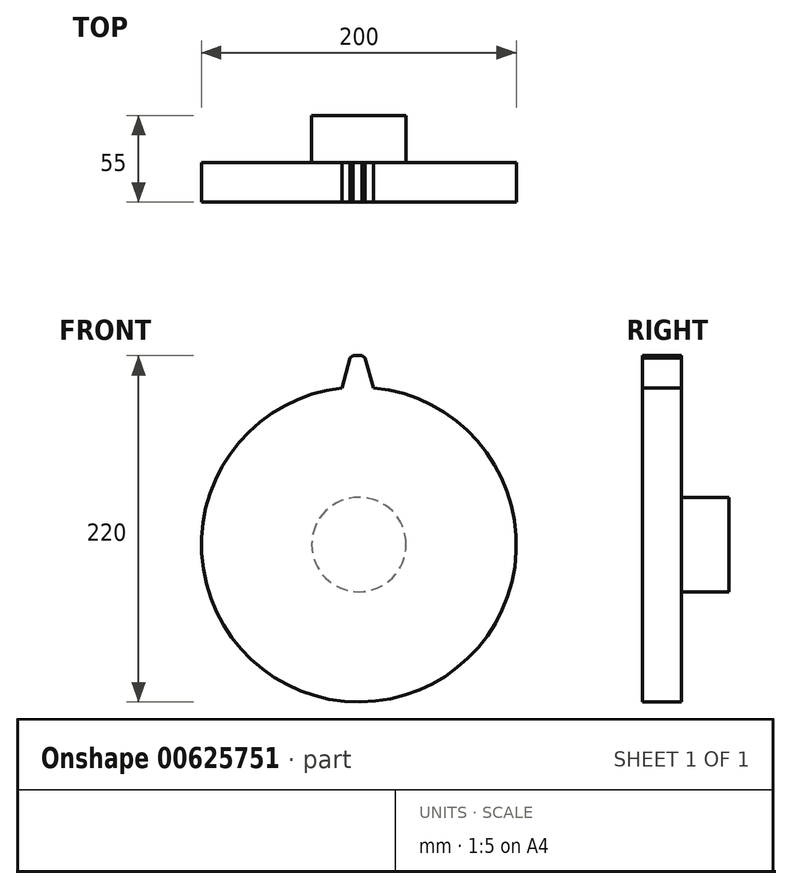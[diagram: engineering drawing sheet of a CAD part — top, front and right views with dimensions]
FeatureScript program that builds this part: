
annotation { "Feature Type Name" : "Feature", "Feature Type Description" : "" }
export const myFeature = defineFeature(function(context is Context, id is Id, definition is map)
    precondition{}
    {
        {
            var Q0;
            Q0=qCreatedBy(makeId("Front.planeOp"),FACE);
            var sketch = newSketch(context, id + "F0", { "sketchPlane" : qUnion([Q0])});
            skCircle(sketch, "E0", {"center": v(0, 0) * mm, "radius": 100 * mm});
            skSolve(sketch);
        }
        {
            var Q0;
            Q0 = qSketchRegion(id + "F0", true);
            extrude(context, id + "F1", {"entities" : qUnion([Q0]), "depth" : 25 * mm, "offsetDistance" : 25 * mm});
        }
        {
            var Q0;
            Q0=makeQuery(id+"F1.opExtrude","CAP_FACE",FACE,{"disambiguationData":[OSD([sQuery(id+"F0.wireOp",EDGE,"E0")])],"isStart":true});
            var sketch = newSketch(context, id + "F2", { "sketchPlane" : qUnion([Q0])});
            skCircle(sketch, "E1", {"center": v(0, 0) * mm, "radius": 30 * mm});
            skSolve(sketch);
        }
        {
            var Q0;
            Q0 = qSketchRegion(id + "F2", true);
            extrude(context, id + "F3", {"entities" : qUnion([Q0]), "operationType" : NewBodyOperationType.ADD, "depth" : 30 * mm, "offsetDistance" : 25 * mm});
        }
        {
            var Q0;
            Q0=makeQuery(id+"F1.opExtrude","CAP_FACE",FACE,{"disambiguationData":[OSD([sQuery(id+"F0.wireOp",EDGE,"E0")])],"isStart":true});
            var sketch = newSketch(context, id + "F4", { "sketchPlane" : qUnion([Q0])});
            skLineSegment(sketch, "E2", {"start": v(-9.33, 99.56) * mm, "end": v(-3.59, 120) * mm});
            skLineSegment(sketch, "E3", {"start": v(-3.59, 120) * mm, "end": v(5.41, 120) * mm});
            skLineSegment(sketch, "E4", {"start": v(5.41, 120) * mm, "end": v(10.66, 99.43) * mm});
            skPoint(sketch, "E5.center", {"position": v(0, 0) * mm});
            skSolve(sketch);
        }
        {
            var Q0;
            Q0 = qSketchRegion(id + "F4", true);
            var Q1;
            {var subQ0=sQuery(id+"F4.wireOp",EDGE,"E2");Q1=makeQuery(id+"F4.imprint","IMPRINT",FACE,{"disambiguationData":[TD([[makeQuery(id+"F4.imprint","IMPRINT",EDGE,{"derivedFrom":subQ0}),-1.0]])]});}
            var Q2;
            {var subQ0=sQuery(id+"F4.wireOp",EDGE,"143b2abc-fa13-4f12-b1d8-8068260f433e.1.0");Q2=makeQuery(id+"F4.imprint","IMPRINT",FACE,{"disambiguationData":[TD([[makeQuery(id+"F4.imprint","IMPRINT",EDGE,{"derivedFrom":subQ0}),-1.0]])]});}
            var Q3;
            {var subQ0=sQuery(id+"F4.wireOp",EDGE,"E5.1.0");Q3=makeQuery(id+"F4.imprint","IMPRINT",FACE,{"disambiguationData":[TD([[makeQuery(id+"F4.imprint","IMPRINT",EDGE,{"derivedFrom":subQ0}),-1.0]])]});}
            var Q4;
            {var subQ0=sQuery(id+"F4.wireOp",EDGE,"E5.2.0");Q4=makeQuery(id+"F4.imprint","IMPRINT",FACE,{"disambiguationData":[TD([[makeQuery(id+"F4.imprint","IMPRINT",EDGE,{"derivedFrom":subQ0}),-1.0]])]});}
            extrude(context, id + "F5", {"entities" : qUnion([Q0, Q1, Q2, Q3, Q4]), "operationType" : NewBodyOperationType.ADD, "oppositeDirection" : true, "depth" : 25 * mm, "offsetDistance" : 25 * mm});
        }
        {
            var Q0;
            Q0=makeQuery(id+"F5.opExtrude","SWEPT_EDGE",EDGE,{"disambiguationData":[OSD([sQuery(id+"F4.wireOp",EDGE,"E2"),sQuery(id+"F4.wireOp",EDGE,"E3")])]});
            var Q1;
            Q1=makeQuery(id+"F5.opExtrude","SWEPT_EDGE",EDGE,{"disambiguationData":[OSD([sQuery(id+"F4.wireOp",EDGE,"E3"),sQuery(id+"F4.wireOp",EDGE,"E4")])]});
            chamfer(context, id + "F6", {"entities" : qUnion([Q0, Q1]), "width" : 2 * mm, "tangentPropagation" : true});
        }
    });
